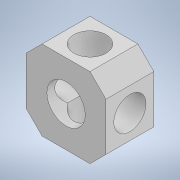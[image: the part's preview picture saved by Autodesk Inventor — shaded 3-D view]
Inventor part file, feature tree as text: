
AUTODESK INVENTOR PART (.ipt)
format: ipt  version: 2022 (Build 260153000, 153)  size: 153,600 bytes
history: native  units: in
note: dims shown in document units (in); Inventor stores cm internally (conversion verified against a paired STEP export)
features: sketch x5, extrude x4, chamfer x1
ambient origin geometry x8: Origin, YZ Plane, XZ Plane, XY Plane, X Axis, Y Axis, Z Axis, Center Point
bodies: Solid1 (feature_tree)
feature tree (10):
  sketch  "Sketch1"  dims[d0=0.9843in d1=0.9843in d2=0.5906in d3=0.0in]
  extrude  "Extrusion1"  Depth=0.9843in
  chamfer  "Chamfer1"  Distance=0.5906in
  extrude  "Extrusion2"  Depth=0.4724in
  extrude  "Extrusion3"  Depth=0.4921in
  extrude  "Extrusion4"  Depth=0.3976in
  sketch  "Sketch2"  dims[d4=0.1969in d5=0.0787in d6=45.0deg d7=0.4724in]
  sketch  "Sketch3"  dims[d8=0.4921in d9=0.4921in]
  sketch  "Sketch4"  dims[d10=0.5906in d11=0.0in d12=0.3976in]
  sketch  "Sketch5"  dims[d13=0.4921in d14=0.2953in d15=0.0in d16=0.0in d17=0.3976in d18=0.2953in d19=0.4921in d20=0.0in d21=0.0in]
